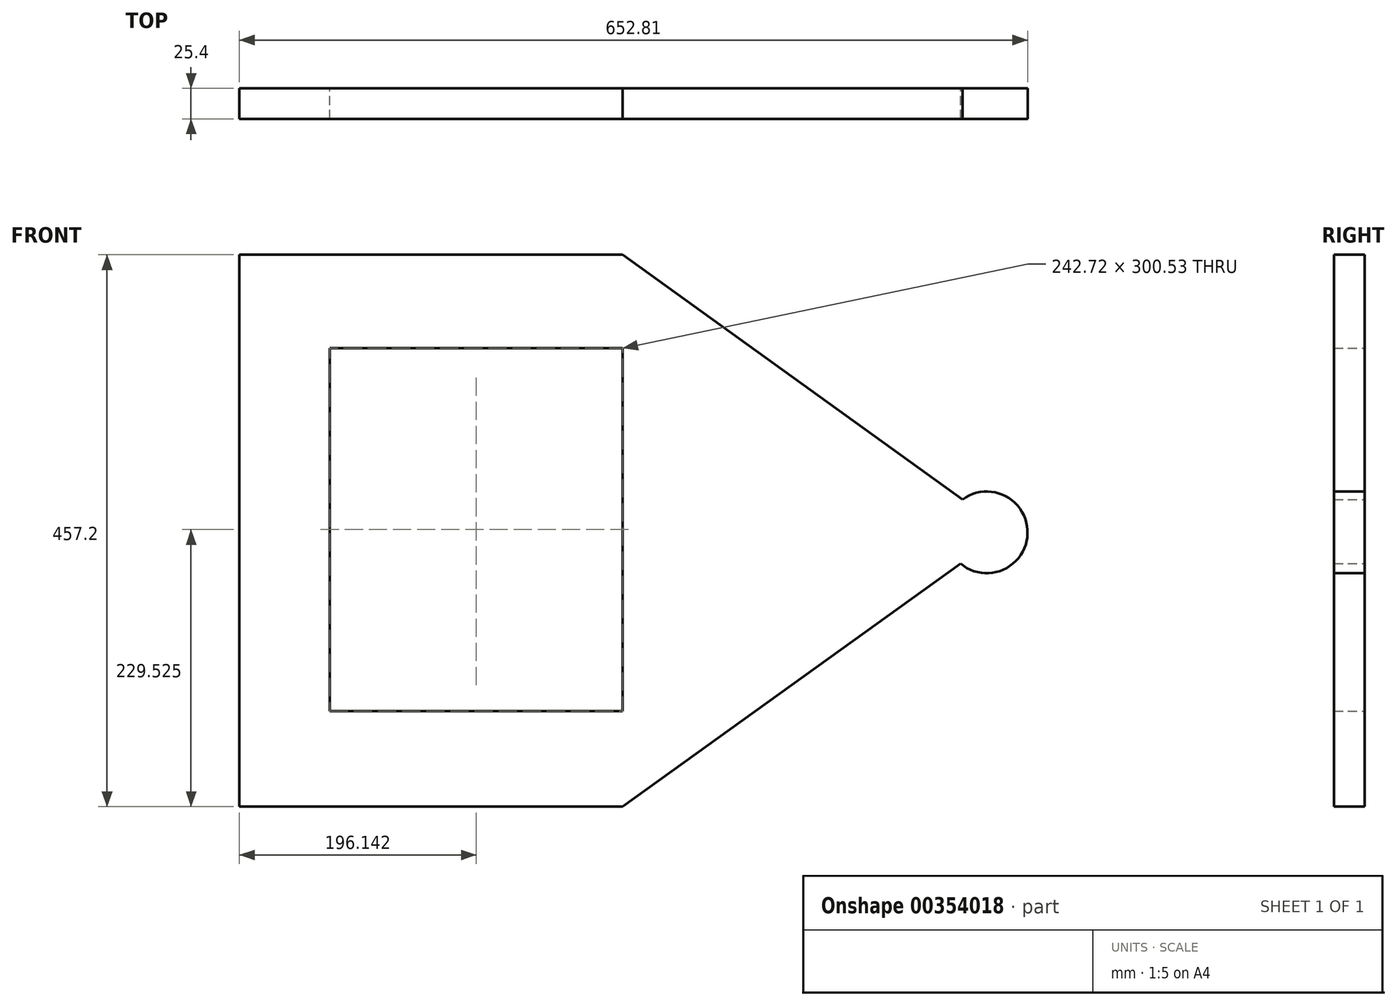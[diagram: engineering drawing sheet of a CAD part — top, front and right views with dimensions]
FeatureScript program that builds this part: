
annotation { "Feature Type Name" : "Feature", "Feature Type Description" : "" }
export const myFeature = defineFeature(function(context is Context, id is Id, definition is map)
    precondition{}
    {
        {
            var Q0;
            Q0=qCreatedBy(makeId("Front.planeOp"),FACE);
            var sketch = newSketch(context, id + "F0", { "sketchPlane" : qUnion([Q0])});
            skLineSegment(sketch, "E0", {"start": v(-438.3, 291.7) * mm, "end": v(-120.8, 291.7) * mm});
            skLineSegment(sketch, "E1", {"start": v(-438.3, 291.7) * mm, "end": v(-438.3, -165.5) * mm});
            skLineSegment(sketch, "E2", {"start": v(-120.8, -165.5) * mm, "end": v(-438.3, -165.5) * mm});
            skPoint(sketch, "E3.orphan", {"position": v(831.7, -165.5) * mm});
            skLineSegment(sketch, "E4", {"start": v(196.7, 91.56) * mm, "end": v(196.7, 32) * mm});
            skLineSegment(sketch, "E5", {"start": v(-120.8, 291.7) * mm, "end": v(196.7, 63.1) * mm});
            skLineSegment(sketch, "E6", {"start": v(-120.8, -165.5) * mm, "end": v(196.7, 63.1) * mm});
            skArc(sketch, "E7", {"start": v(158.94, 35.91) * mm, "mid": v(214.49, 60.66) * mm, "end": v(160.7, 89.01) * mm});
            skPoint(sketch, "E8.orphan", {"position": v(196.7, 291.7) * mm});
            skPoint(sketch, "E9.orphan", {"position": v(196.7, -165.5) * mm});
            skLineSegment(sketch, "E10.bottom", {"start": v(-120.8, -86.25) * mm, "end": v(-363.53, -86.25) * mm});
            skLineSegment(sketch, "E10.top", {"start": v(-120.8, 214.28) * mm, "end": v(-363.53, 214.28) * mm});
            skLineSegment(sketch, "E10.left", {"start": v(-120.8, -86.25) * mm, "end": v(-120.8, 214.28) * mm});
            skLineSegment(sketch, "E10.right", {"start": v(-363.53, -86.25) * mm, "end": v(-363.53, 214.28) * mm});
            skSolve(sketch);
        }
        {
            var Q0;
            Q0 = qSketchRegion(id + "F0", true);
            extrude(context, id + "F1", {"entities" : qUnion([Q0]), "depth" : 25.4 * mm});
        }
    });
